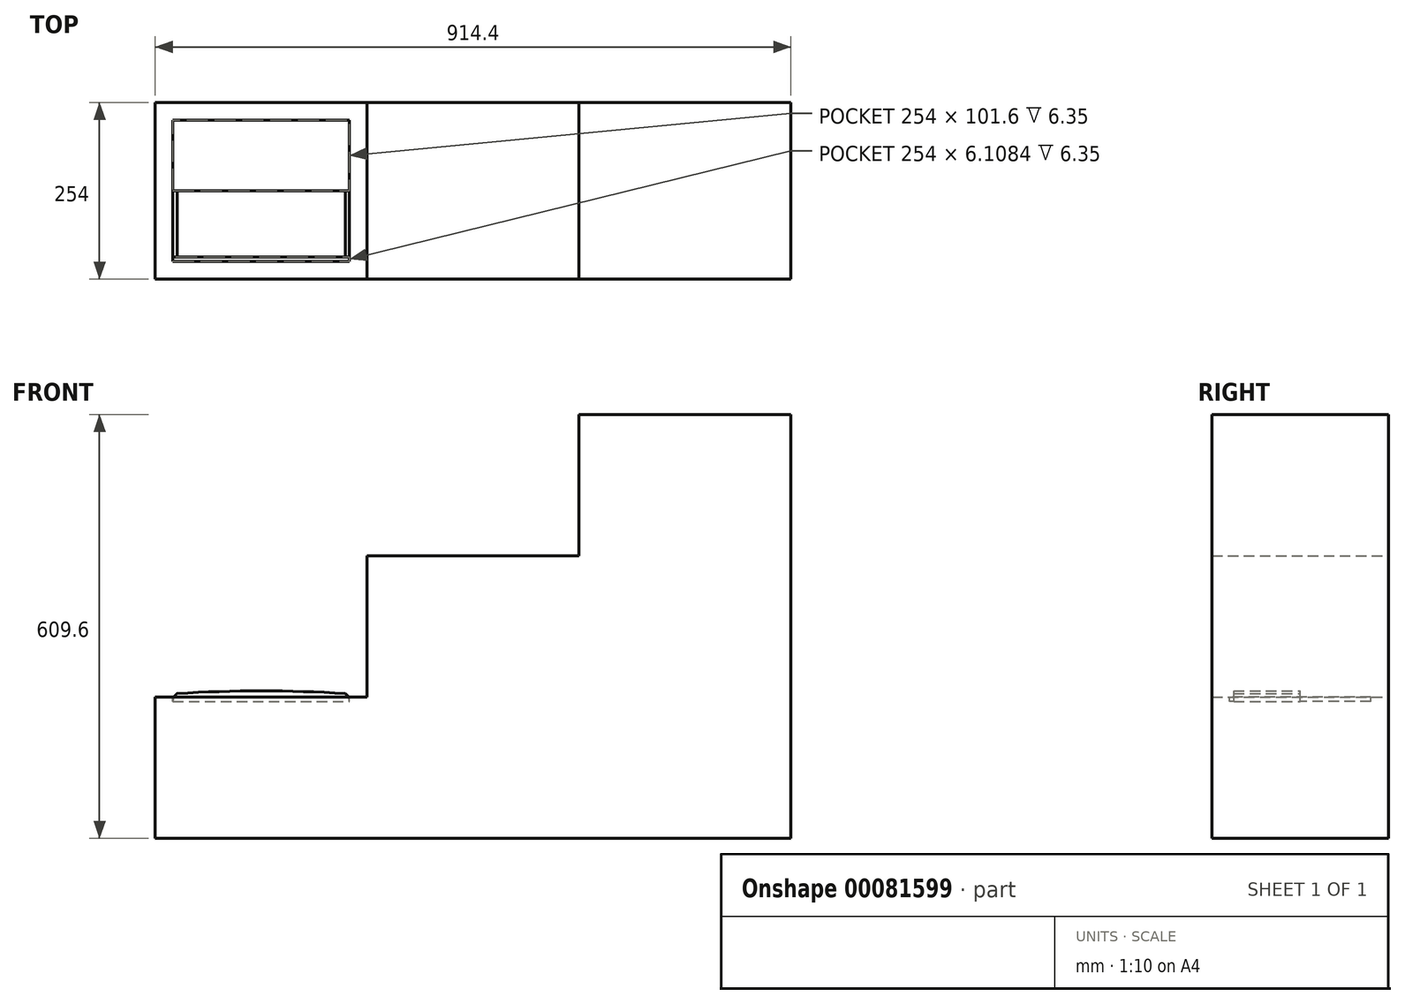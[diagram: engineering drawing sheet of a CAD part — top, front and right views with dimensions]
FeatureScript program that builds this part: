
annotation { "Feature Type Name" : "Feature", "Feature Type Description" : "" }
export const myFeature = defineFeature(function(context is Context, id is Id, definition is map)
    precondition{}
    {
        {
            var Q0;
            Q0=qCreatedBy(makeId("Front.planeOp"),FACE);
            var sketch = newSketch(context, id + "F0", { "sketchPlane" : qUnion([Q0])});
            skLineSegment(sketch, "E0.bottom", {"start": v(0, 0) * mm, "end": v(914.4, 0) * mm});
            skLineSegment(sketch, "E0.top", {"start": v(0, 203.2) * mm, "end": v(914.4, 203.2) * mm});
            skLineSegment(sketch, "E0.left", {"start": v(0, 0) * mm, "end": v(0, 203.2) * mm});
            skLineSegment(sketch, "E0.right", {"start": v(914.4, 0) * mm, "end": v(914.4, 203.2) * mm});
            skLineSegment(sketch, "E1", {"start": v(0, 203.2) * mm, "end": v(0, 406.4) * mm, "construction": true});
            skLineSegment(sketch, "E2", {"start": v(0, 406.4) * mm, "end": v(304.8, 406.4) * mm, "construction": true});
            skLineSegment(sketch, "E3.bottom", {"start": v(304.8, 406.4) * mm, "end": v(609.6, 406.4) * mm});
            skLineSegment(sketch, "E3.top", {"start": v(304.8, 203.2) * mm, "end": v(609.6, 203.2) * mm});
            skLineSegment(sketch, "E3.left", {"start": v(304.8, 406.4) * mm, "end": v(304.8, 203.2) * mm});
            skLineSegment(sketch, "E3.right", {"start": v(609.6, 406.4) * mm, "end": v(609.6, 203.2) * mm});
            skLineSegment(sketch, "E4", {"start": v(609.6, 406.4) * mm, "end": v(609.6, 609.6) * mm, "construction": true});
            skLineSegment(sketch, "E5.bottom", {"start": v(609.6, 609.6) * mm, "end": v(914.4, 609.6) * mm});
            skLineSegment(sketch, "E5.top", {"start": v(609.6, 203.2) * mm, "end": v(914.4, 203.2) * mm});
            skLineSegment(sketch, "E5.left", {"start": v(609.6, 609.6) * mm, "end": v(609.6, 203.2) * mm});
            skLineSegment(sketch, "E5.right", {"start": v(914.4, 609.6) * mm, "end": v(914.4, 203.2) * mm});
            skLineSegment(sketch, "E6", {"start": v(609.6, 406.4) * mm, "end": v(914.4, 406.4) * mm, "construction": true});
            skLineSegment(sketch, "E7", {"start": v(609.6, 203.2) * mm, "end": v(609.6, 0) * mm, "construction": true});
            skLineSegment(sketch, "E8", {"start": v(304.8, 203.2) * mm, "end": v(304.8, 0) * mm, "construction": true});
            skSolve(sketch);
        }
        {
            var Q0;
            {var subQ0=sQuery(id+"F0.wireOp",EDGE,"E3.bottom");Q0=makeQuery(id+"F0.imprint","IMPRINT",FACE,{"disambiguationData":[TD([[makeQuery(id+"F0.imprint","IMPRINT",EDGE,{"derivedFrom":subQ0}),-1.0]])]});}
            var Q1;
            {var subQ3=sQuery(id+"F0.wireOp",EDGE,"E5.bottom");Q1=makeQuery(id+"F0.imprint","IMPRINT",FACE,{"disambiguationData":[TD([[makeQuery(id+"F0.imprint","IMPRINT",EDGE,{"derivedFrom":subQ3}),-1.0]])]});}
            var Q2;
            Q2=makeQuery(id+"F0.imprint","IMPRINT",FACE,{"disambiguationData":[TD([[makeQuery(id+"F0.imprint","IMPRINT",EDGE,{"derivedFrom":sQuery(id+"F0.wireOp",EDGE,"E0.bottom")}),1.0]])]});
            extrude(context, id + "F1", {"entities" : qUnion([Q0, Q1, Q2]), "depth" : 254 * mm});
        }
        {
            var Q0;
            Q0=makeQuery(id+"F1.opExtrude","SWEPT_FACE",FACE,{"disambiguationData":[OSD([sQuery(id+"F0.wireOp",EDGE,"E0.top")])]});
            var sketch = newSketch(context, id + "F2", { "sketchPlane" : qUnion([Q0])});
            skLineSegment(sketch, "E9", {"start": v(152.4, 0) * mm, "end": v(152.4, -254) * mm, "construction": true});
            skLineSegment(sketch, "E10", {"start": v(0, -127) * mm, "end": v(304.8, -127) * mm, "construction": true});
            skLineSegment(sketch, "E11.bottom", {"start": v(279.4, -25.4) * mm, "end": v(25.4, -25.4) * mm});
            skLineSegment(sketch, "E11.top", {"start": v(279.4, -228.6) * mm, "end": v(25.4, -228.6) * mm});
            skLineSegment(sketch, "E11.left", {"start": v(279.4, -25.4) * mm, "end": v(279.4, -228.6) * mm});
            skLineSegment(sketch, "E11.right", {"start": v(25.4, -25.4) * mm, "end": v(25.4, -228.6) * mm});
            skPoint(sketch, "E11.middle", {"position": v(152.4, -127) * mm});
            skSolve(sketch);
        }
        {
            var Q0;
            Q0=makeQuery(id+"F2.imprint","IMPRINT",FACE,{"disambiguationData":[TD([[makeQuery(id+"F2.imprint","IMPRINT",EDGE,{"derivedFrom":sQuery(id+"F2.wireOp",EDGE,"E11.bottom")}),1.0]])]});
            extrude(context, id + "F3", {"entities" : qUnion([Q0]), "operationType" : NewBodyOperationType.REMOVE, "oppositeDirection" : true, "depth" : 6.35 * mm});
        }
        {
            var Q0;
            Q0=qCreatedBy(makeId("Front.planeOp"),FACE);
            cPlane(context, id + "F4", {"entities" : qUnion([Q0]), "cplaneType" : CPlaneType.OFFSET, "offset" : 127 * mm, "width" : 152.4 * mm, "height" : 152.4 * mm});
        }
        {
            var Q0;
            Q0=qCreatedBy(makeId("Right.planeOp"),FACE);
            cPlane(context, id + "F5", {"entities" : qUnion([Q0]), "cplaneType" : CPlaneType.OFFSET, "offset" : 31.5 * mm, "width" : 152.4 * mm, "height" : 152.4 * mm});
        }
        {
            var Q0;
            Q0=qCreatedBy(id+"F4.planeOp",FACE);
            var sketch = newSketch(context, id + "F6", { "sketchPlane" : qUnion([Q0])});
            skPoint(sketch, "E12", {"position": v(25.4, 203.2) * mm});
            skLineSegment(sketch, "E13", {"start": v(25.4, 203.2) * mm, "end": v(25.4, 196.85) * mm, "construction": true});
            skLineSegment(sketch, "E14", {"start": v(25.4, 203.2) * mm, "end": v(50.8, 203.2) * mm, "construction": true});
            skLineSegment(sketch, "E15", {"start": v(25.4, 196.85) * mm, "end": v(25.4, 203.2) * mm, "construction": true});
            skLineSegment(sketch, "E16", {"start": v(31.5, 203.2) * mm, "end": v(31.5, 208.28) * mm, "construction": true});
            skArc(sketch, "E17", {"start": v(31.5, 208.28) * mm, "mid": v(27.02, 203.33) * mm, "end": v(25.4, 196.85) * mm});
            skPoint(sketch, "E18", {"position": v(279.4, 203.2) * mm});
            skLineSegment(sketch, "E19", {"start": v(279.4, 203.2) * mm, "end": v(279.4, 196.85) * mm, "construction": true});
            skLineSegment(sketch, "E20", {"start": v(279.4, 196.85) * mm, "end": v(279.4, 203.2) * mm, "construction": true});
            skArc(sketch, "E21", {"start": v(279.4, 196.85) * mm, "mid": v(277.78, 203.33) * mm, "end": v(273.3, 208.28) * mm});
            skLineSegment(sketch, "E22", {"start": v(279.4, 203.2) * mm, "end": v(273.04, 203.2) * mm, "construction": true});
            skLineSegment(sketch, "E23", {"start": v(31.5, 208.28) * mm, "end": v(273.3, 208.28) * mm, "construction": true});
            skArc(sketch, "E24", {"start": v(273.3, 208.28) * mm, "mid": v(152.4, 212.12) * mm, "end": v(31.5, 208.28) * mm});
            skLineSegment(sketch, "E25", {"start": v(25.4, 196.85) * mm, "end": v(279.4, 196.85) * mm});
            skSolve(sketch);
        }
        {
            var Q0;
            Q0 = qSketchRegion(id + "F6", true);
            extrude(context, id + "F7", {"entities" : qUnion([Q0]), "operationType" : NewBodyOperationType.ADD, "depth" : 101.6 * mm - 6.1 * mm});
        }
    });
